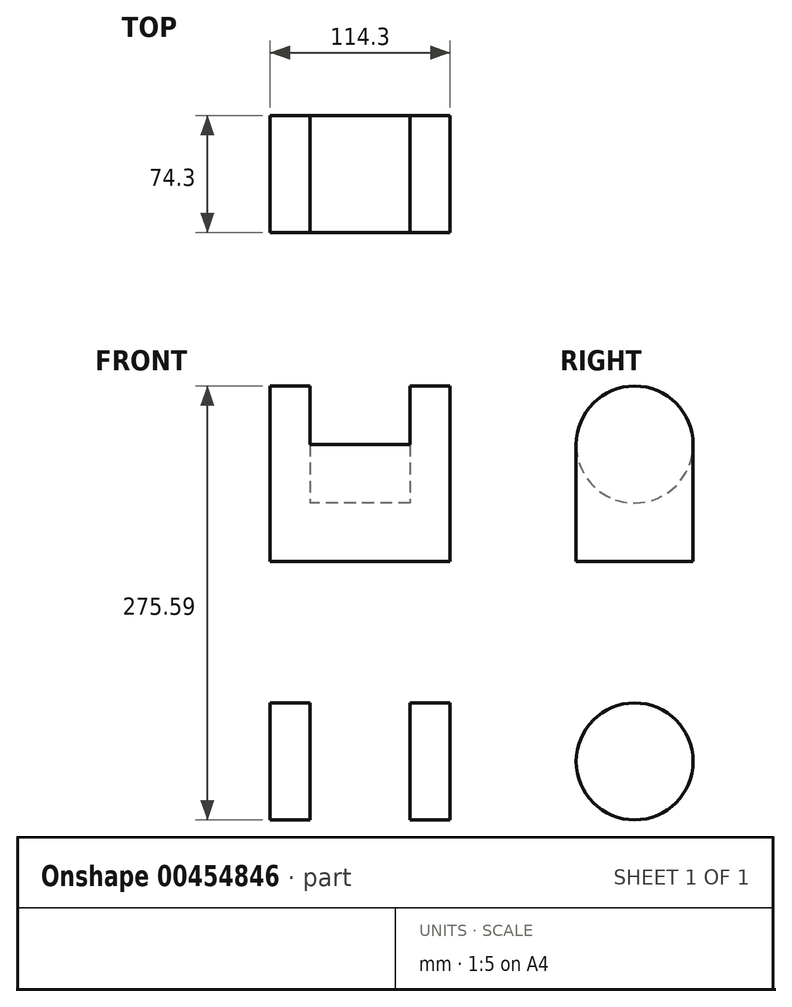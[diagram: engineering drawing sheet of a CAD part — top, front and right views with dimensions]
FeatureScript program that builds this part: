
annotation { "Feature Type Name" : "Feature", "Feature Type Description" : "" }
export const myFeature = defineFeature(function(context is Context, id is Id, definition is map)
    precondition{}
    {
        {
            var Q0;
            Q0=qCreatedBy(makeId("Right.planeOp"),FACE);
            var sketch = newSketch(context, id + "F0", { "sketchPlane" : qUnion([Q0])});
            skCircle(sketch, "E0", {"center": v(0, 0) * mm, "radius": 37.15 * mm});
            skLineSegment(sketch, "E1.bottom", {"start": v(37.15, 0) * mm, "end": v(-37.15, 0) * mm});
            skLineSegment(sketch, "E1.top", {"start": v(37.15, -74.3) * mm, "end": v(-37.15, -74.3) * mm});
            skLineSegment(sketch, "E1.left", {"start": v(37.15, 0) * mm, "end": v(37.15, -74.3) * mm});
            skLineSegment(sketch, "E1.right", {"start": v(-37.15, 0) * mm, "end": v(-37.15, -74.3) * mm});
            skPoint(sketch, "E1.middle", {"position": v(0, -37.15) * mm});
            skLineSegment(sketch, "E2.bottom", {"start": v(-37.15, -74.3) * mm, "end": v(37.15, -74.3) * mm});
            skLineSegment(sketch, "E2.top", {"start": v(-37.15, -201.3) * mm, "end": v(37.15, -201.3) * mm});
            skLineSegment(sketch, "E2.left", {"start": v(-37.15, -74.3) * mm, "end": v(-37.15, -155.8) * mm});
            skLineSegment(sketch, "E2.right", {"start": v(37.15, -74.3) * mm, "end": v(37.15, -201.3) * mm});
            skCircle(sketch, "E3", {"center": v(0, -201.3) * mm, "radius": 37.15 * mm});
            skLineSegment(sketch, "E4", {"start": v(-37.15, -155.8) * mm, "end": v(0, -163.38) * mm});
            skLineSegment(sketch, "E5", {"start": v(0, -163.38) * mm, "end": v(37.15, -201.3) * mm});
            skSolve(sketch);
        }
        {
            var Q0;
            {var subQ0=sQuery(id+"F0.wireOp",EDGE,"E1.left");Q0=makeQuery(id+"F0.imprint","IMPRINT",FACE,{"disambiguationData":[TD([[makeQuery(id+"F0.imprint","IMPRINT",EDGE,{"derivedFrom":subQ0}),-1.0]])]});}
            var Q1;
            {var subQ6=sQuery(id+"F0.wireOp",EDGE,"E2.bottom");Q1=makeQuery(id+"F0.imprint","IMPRINT",FACE,{"disambiguationData":[TD([[makeQuery(id+"F0.imprint","IMPRINT",EDGE,{"derivedFrom":subQ6}),-1.0]])]});}
            extrude(context, id + "F1", {"entities" : qUnion([Q0, Q1]), "endBound" : BoundingType.SYMMETRIC, "depth" : 114.3 * mm, "offsetDistance" : 25.4 * mm});
        }
        {
            var Q0;
            {var subQ0=sQuery(id+"F0.wireOp",EDGE,"E1.bottom");Q0=makeQuery(id+"F0.imprint","IMPRINT",FACE,{"disambiguationData":[TD([[makeQuery(id+"F0.imprint","IMPRINT",EDGE,{"derivedFrom":subQ0}),-1.0]])]});}
            var Q1;
            {var subQ0=sQuery(id+"F0.wireOp",EDGE,"E1.bottom");Q1=makeQuery(id+"F0.imprint","IMPRINT",FACE,{"disambiguationData":[TD([[makeQuery(id+"F0.imprint","IMPRINT",EDGE,{"derivedFrom":subQ0}),1.0]])]});}
            extrude(context, id + "F2", {"entities" : qUnion([Q0, Q1]), "operationType" : NewBodyOperationType.ADD, "depth" : 57.15 * mm, "offsetDistance" : 25.4 * mm, "hasSecondDirection" : true, "secondDirectionOppositeDirection" : false, "secondDirectionDepth" : 31.75 * mm});
        }
        {
            var Q0;
            {var subQ0=sQuery(id+"F0.wireOp",EDGE,"E1.bottom");Q0=makeQuery(id+"F0.imprint","IMPRINT",FACE,{"disambiguationData":[TD([[makeQuery(id+"F0.imprint","IMPRINT",EDGE,{"derivedFrom":subQ0}),-1.0]])]});}
            var Q1;
            {var subQ0=sQuery(id+"F0.wireOp",EDGE,"E1.bottom");Q1=makeQuery(id+"F0.imprint","IMPRINT",FACE,{"disambiguationData":[TD([[makeQuery(id+"F0.imprint","IMPRINT",EDGE,{"derivedFrom":subQ0}),1.0]])]});}
            extrude(context, id + "F3", {"entities" : qUnion([Q0, Q1]), "operationType" : NewBodyOperationType.ADD, "oppositeDirection" : true, "depth" : 57.15 * mm, "offsetDistance" : 25.4 * mm, "hasSecondDirection" : true, "secondDirectionOppositeDirection" : true, "secondDirectionDepth" : 31.75 * mm});
        }
        {
            var Q0;
            {var subQ0=sQuery(id+"F0.wireOp",EDGE,"E2.top");Q0=makeQuery(id+"F0.imprint","IMPRINT",FACE,{"disambiguationData":[TD([[makeQuery(id+"F0.imprint","IMPRINT",EDGE,{"derivedFrom":subQ0}),1.0]])]});}
            var Q1;
            {var subQ0=sQuery(id+"F0.wireOp",EDGE,"E2.top");Q1=makeQuery(id+"F0.imprint","IMPRINT",FACE,{"disambiguationData":[TD([[makeQuery(id+"F0.imprint","IMPRINT",EDGE,{"derivedFrom":subQ0}),-1.0]])]});}
            var Q2;
            {var subQ0=sQuery(id+"F0.wireOp",EDGE,"E5");var subQ1=sQuery(id+"F0.wireOp",EDGE,"E3");var subQ3=makeQuery(id+"F0.imprint","INTERSECT",VERTEX,{"derivedFrom":[subQ1,subQ0]});Q2=makeQuery(id+"F0.imprint","IMPRINT",FACE,{"disambiguationData":[TD([[makeQuery(id+"F0.imprint","IMPRINT",EDGE,{"disambiguationData":[TD([[subQ3,1.0]])],"derivedFrom":subQ1}),1.0]])]});}
            extrude(context, id + "F4", {"entities" : qUnion([Q0, Q1, Q2]), "operationType" : NewBodyOperationType.ADD, "depth" : 57.15 * mm, "offsetDistance" : 25.4 * mm, "hasSecondDirection" : true, "secondDirectionOppositeDirection" : false, "secondDirectionDepth" : 31.75 * mm});
        }
        {
            var Q0;
            {var subQ0=sQuery(id+"F0.wireOp",EDGE,"E2.top");Q0=makeQuery(id+"F0.imprint","IMPRINT",FACE,{"disambiguationData":[TD([[makeQuery(id+"F0.imprint","IMPRINT",EDGE,{"derivedFrom":subQ0}),1.0]])]});}
            var Q1;
            {var subQ0=sQuery(id+"F0.wireOp",EDGE,"E2.top");Q1=makeQuery(id+"F0.imprint","IMPRINT",FACE,{"disambiguationData":[TD([[makeQuery(id+"F0.imprint","IMPRINT",EDGE,{"derivedFrom":subQ0}),-1.0]])]});}
            var Q2;
            {var subQ0=sQuery(id+"F0.wireOp",EDGE,"E5");var subQ1=sQuery(id+"F0.wireOp",EDGE,"E3");var subQ3=makeQuery(id+"F0.imprint","INTERSECT",VERTEX,{"derivedFrom":[subQ1,subQ0]});Q2=makeQuery(id+"F0.imprint","IMPRINT",FACE,{"disambiguationData":[TD([[makeQuery(id+"F0.imprint","IMPRINT",EDGE,{"disambiguationData":[TD([[subQ3,1.0]])],"derivedFrom":subQ1}),1.0]])]});}
            extrude(context, id + "F5", {"entities" : qUnion([Q0, Q1, Q2]), "operationType" : NewBodyOperationType.ADD, "oppositeDirection" : true, "depth" : 57.15 * mm, "offsetDistance" : 25.4 * mm, "hasSecondDirection" : true, "secondDirectionOppositeDirection" : true, "secondDirectionDepth" : 31.75 * mm});
        }
    });
